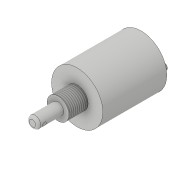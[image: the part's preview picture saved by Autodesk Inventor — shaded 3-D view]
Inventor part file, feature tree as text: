
AUTODESK INVENTOR PART (.ipt)
format: ipt  version: 2019 (Build 230136000, 136)  size: 120,320 bytes
history: native  units: mm
features: extrude x5, sketch x5, thread x1, fillet x1
ambient origin geometry x8: Origin, YZ Plane, XZ Plane, XY Plane, X Axis, Y Axis, Z Axis, Center Point
bodies: Solid1 (feature_tree)
feature tree (12):
  extrude  "Extrusion1"  Depth=50.0mm TaperAngle=0.0deg
  extrude  "Extrusion2"  Depth=15.0mm TaperAngle=0.0deg
  thread  "Thread1"  [1 undecoded]
  extrude  "Extrusion3"  Depth=20.0mm TaperAngle=0.0deg
  extrude  "Extrusion4"  Depth=5.0mm
  fillet  "Fillet1"  [1 undecoded]
  extrude  "Extrusion5"  Depth=5.0mm
  sketch  "Sketch1"  dims[d0=40.0mm d1=50.0mm d2=0.0mm]
  sketch  "Sketch2"  dims[d3=17.0mm d4=15.0mm d5=0.0mm d6=10.0mm d7=0.0mm]
  sketch  "Sketch3"  dims[d8=9.0mm d9=20.0mm d10=0.0mm]
  sketch  "Sketch4"  dims[d11=5.0mm d12=3.0mm d13=0.0mm d14=0.0mm]
  sketch  "Sketch5"  dims[d15=2.0mm d16=5.0mm d17=5.0mm d18=5.0mm d19=0.0mm]
note: 2 required parameter values undecoded (feature->parameter linkage not recoverable at this tier; creation-order binding heuristic only, values carry confidence <= 0.55)
